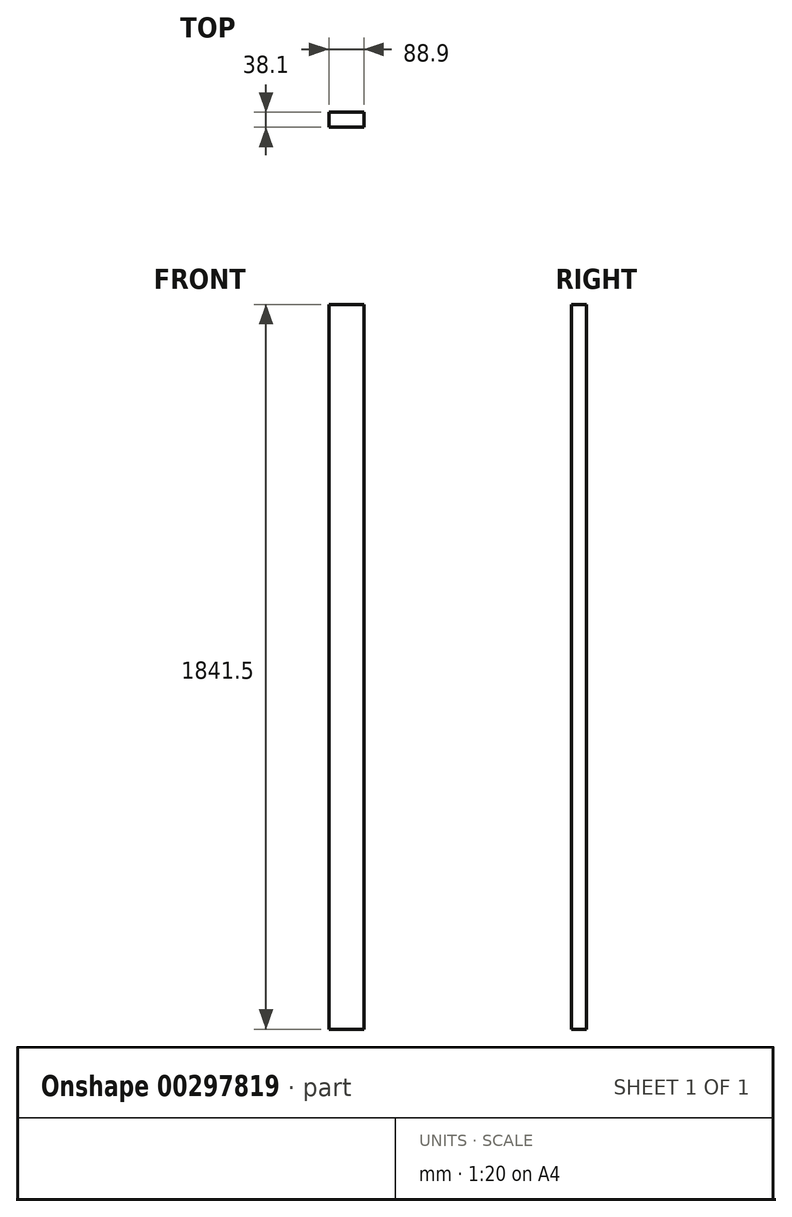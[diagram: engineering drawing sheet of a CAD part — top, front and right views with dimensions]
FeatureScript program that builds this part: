
annotation { "Feature Type Name" : "Feature", "Feature Type Description" : "" }
export const myFeature = defineFeature(function(context is Context, id is Id, definition is map)
    precondition{}
    {
        {
            var Q0;
            Q0=qCreatedBy(makeId("Top.planeOp"),FACE);
            var sketch = newSketch(context, id + "F0", { "sketchPlane" : qUnion([Q0])});
            skLineSegment(sketch, "E0.bottom", {"start": v(0, 0) * mm, "end": v(88.9, 0) * mm});
            skLineSegment(sketch, "E0.top", {"start": v(0, 38.1) * mm, "end": v(88.9, 38.1) * mm});
            skLineSegment(sketch, "E0.left", {"start": v(0, 0) * mm, "end": v(0, 38.1) * mm});
            skLineSegment(sketch, "E0.right", {"start": v(88.9, 0) * mm, "end": v(88.9, 38.1) * mm});
            skSolve(sketch);
        }
        {
            var Q0;
            Q0=makeQuery(id+"F0.imprint","IMPRINT",FACE,{"disambiguationData":[TD([[makeQuery(id+"F0.imprint","IMPRINT",EDGE,{"derivedFrom":sQuery(id+"F0.wireOp",EDGE,"E0.bottom")}),1.0]])]});
            extrude(context, id + "F1", {"entities" : qUnion([Q0]), "depth" : 1841.5 * mm});
        }
    });
